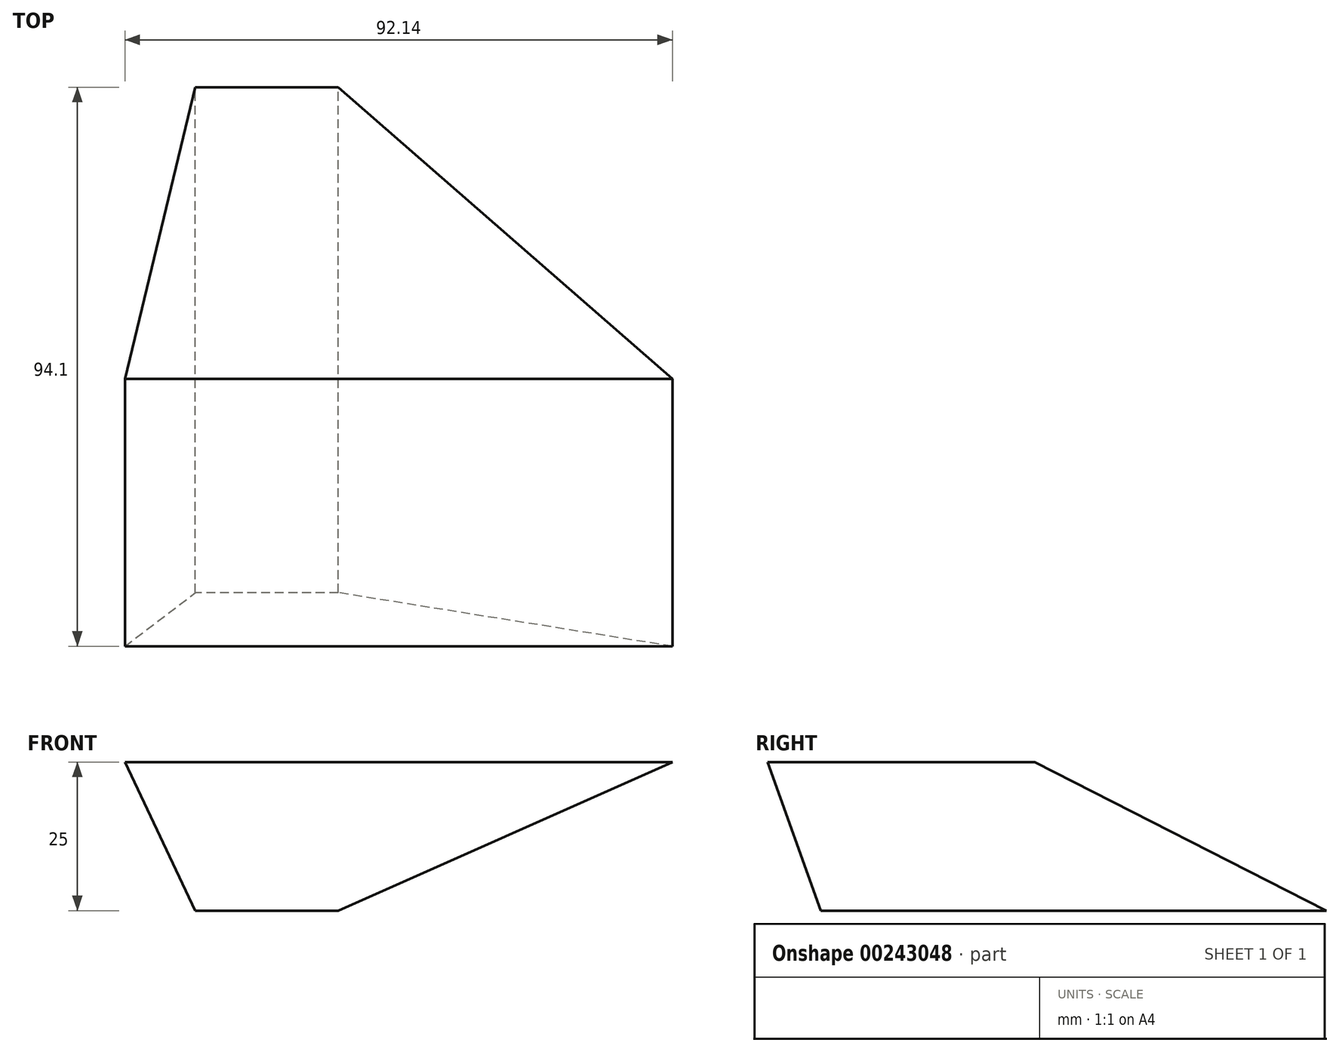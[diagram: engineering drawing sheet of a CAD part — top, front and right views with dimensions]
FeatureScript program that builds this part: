
annotation { "Feature Type Name" : "Feature", "Feature Type Description" : "" }
export const myFeature = defineFeature(function(context is Context, id is Id, definition is map)
    precondition{}
    {
        {
            var Q0;
            Q0=qCreatedBy(makeId("Top.planeOp"),FACE);
            var sketch = newSketch(context, id + "F0", { "sketchPlane" : qUnion([Q0])});
            skLineSegment(sketch, "E0.bottom", {"start": v(0, -35.98) * mm, "end": v(-24.05, -35.98) * mm});
            skLineSegment(sketch, "E0.top", {"start": v(0, 49.11) * mm, "end": v(-24.05, 49.11) * mm});
            skLineSegment(sketch, "E0.left", {"start": v(0, -35.98) * mm, "end": v(0, 49.11) * mm});
            skLineSegment(sketch, "E0.right", {"start": v(-24.05, -35.98) * mm, "end": v(-24.05, 49.11) * mm});
            skSolve(sketch);
        }
        {
            var Q0;
            Q0=qCreatedBy(makeId("Top.planeOp"),FACE);
            cPlane(context, id + "F1", {"entities" : qUnion([Q0]), "cplaneType" : CPlaneType.OFFSET, "offset" : 25 * mm, "width" : 150 * mm, "height" : 150 * mm});
        }
        {
            var Q0;
            Q0=qCreatedBy(id+"F1.planeOp",FACE);
            var sketch = newSketch(context, id + "F2", { "sketchPlane" : qUnion([Q0])});
            skLineSegment(sketch, "E1.bottom", {"start": v(-35.92, -45) * mm, "end": v(56.22, -45) * mm});
            skLineSegment(sketch, "E1.top", {"start": v(-35.92, 0) * mm, "end": v(56.22, 0) * mm});
            skLineSegment(sketch, "E1.left", {"start": v(-35.92, -45) * mm, "end": v(-35.92, 0) * mm});
            skLineSegment(sketch, "E1.right", {"start": v(56.22, -45) * mm, "end": v(56.22, 0) * mm});
            skSolve(sketch);
        }
        {
            var Q0;
            Q0 = qSketchRegion(id + "F2", true);
            var Q1;
            Q1 = qSketchRegion(id + "F0", true);
            loft(context, id + "F3", {"sheetProfilesArray" : [{ "sheetProfileEntities" : qUnion([Q0]) }, { "sheetProfileEntities" : qUnion([Q1]) }]});
        }
    });
